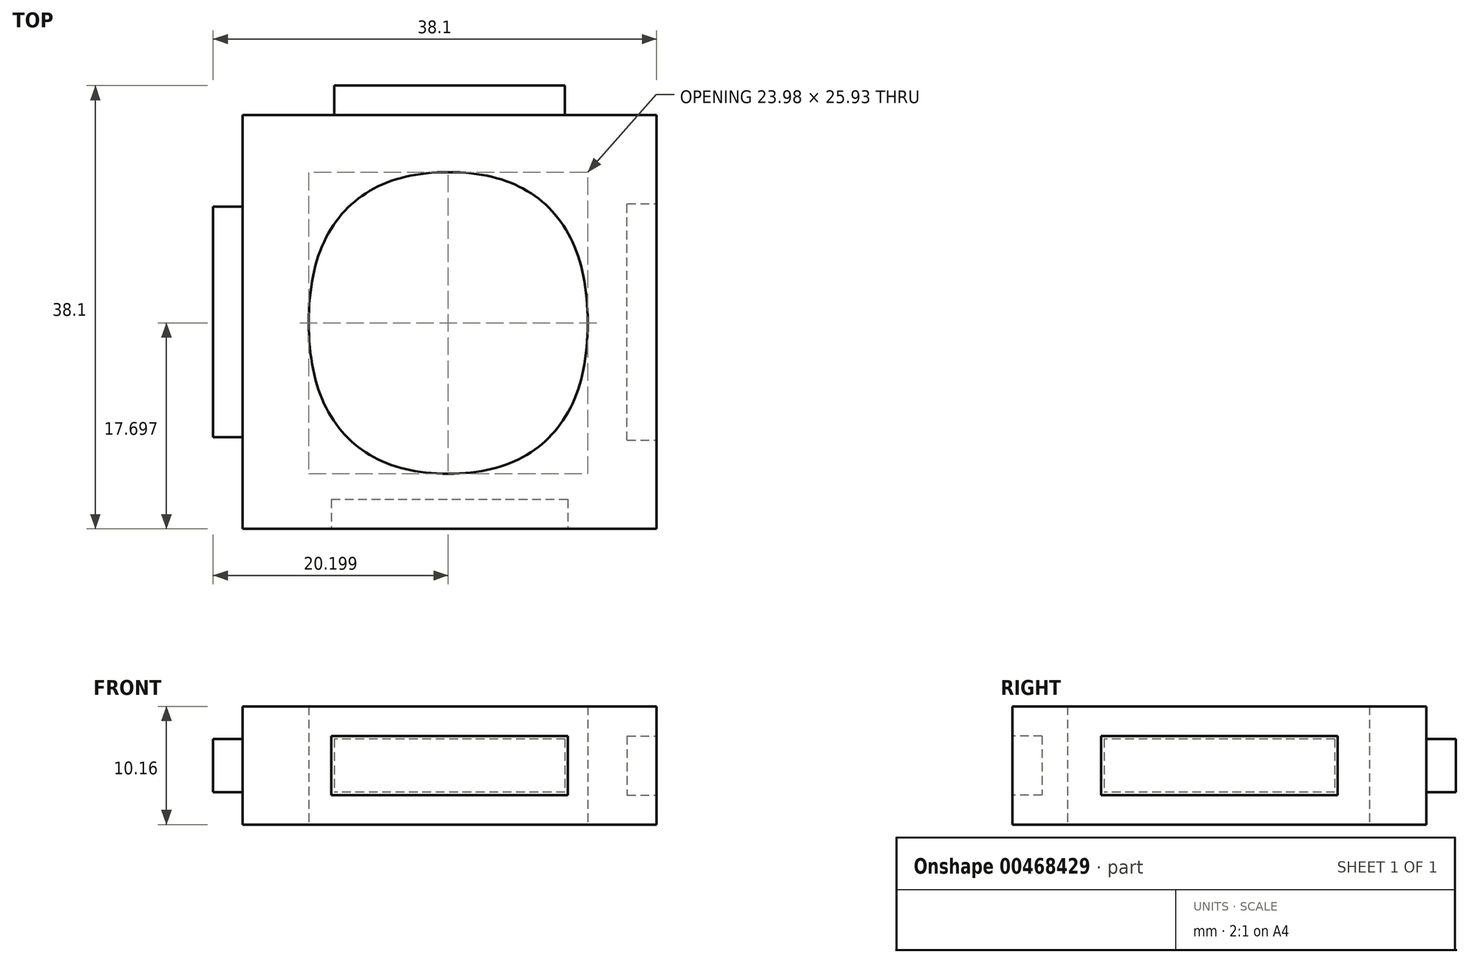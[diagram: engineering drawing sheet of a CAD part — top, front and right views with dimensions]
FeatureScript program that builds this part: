
annotation { "Feature Type Name" : "Feature", "Feature Type Description" : "" }
export const myFeature = defineFeature(function(context is Context, id is Id, definition is map)
    precondition{}
    {
        {
            var Q0;
            Q0=qCreatedBy(makeId("Top.planeOp"),FACE);
            var sketch = newSketch(context, id + "F0", { "sketchPlane" : qUnion([Q0])});
            skLineSegment(sketch, "E0.bottom", {"start": v(-17.78, 17.78) * mm, "end": v(17.78, 17.78) * mm});
            skLineSegment(sketch, "E0.top", {"start": v(-17.78, -17.78) * mm, "end": v(17.78, -17.78) * mm});
            skLineSegment(sketch, "E0.left", {"start": v(-17.78, 17.78) * mm, "end": v(-17.78, -17.78) * mm});
            skLineSegment(sketch, "E0.right", {"start": v(17.78, 17.78) * mm, "end": v(17.78, -17.78) * mm});
            skText(sketch, "E1", { "text": "O", "fontName": "OpenSans-Bold.ttf"});
            const initialGuessF0  = {"E1": [-0.01416, -0.0127, 1, 0, 0.0254]};
            skSetInitialGuess(sketch, initialGuessF0);
            skSolve(sketch);
        }
        {
            var Q0;
            Q0=qSketchRegion(id+"F0",true);
            extrude(context, id + "F1", {"entities" : qUnion([Q0]), "endBound" : BoundingType.SYMMETRIC, "depth" : 10.16 * mm});
        }
        {
            var Q0;
            Q0=makeQuery(id+"F1.opExtrude","SWEPT_FACE",FACE,{"disambiguationData":[OSD([sQuery(id+"F0.wireOp",EDGE,"E0.bottom")])]});
            var sketch = newSketch(context, id + "F2", { "sketchPlane" : qUnion([Q0])});
            skLineSegment(sketch, "E2.bottom", {"start": v(-9.9, 2.29) * mm, "end": v(9.9, 2.29) * mm});
            skLineSegment(sketch, "E2.top", {"start": v(-9.9, -2.29) * mm, "end": v(9.9, -2.29) * mm});
            skLineSegment(sketch, "E2.left", {"start": v(-9.9, 2.29) * mm, "end": v(-9.9, -2.29) * mm});
            skLineSegment(sketch, "E2.right", {"start": v(9.9, 2.29) * mm, "end": v(9.9, -2.29) * mm});
            skSolve(sketch);
        }
        {
            var Q0;
            Q0=qSketchRegion(id+"F2",true);
            extrude(context, id + "F3", {"entities" : qUnion([Q0]), "operationType" : NewBodyOperationType.ADD, "depth" : 2.54 * mm});
        }
        {
            var Q0;
            Q0=makeQuery(id+"F1.opExtrude","SWEPT_FACE",FACE,{"disambiguationData":[OSD([sQuery(id+"F0.wireOp",EDGE,"E0.left")])]});
            var sketch = newSketch(context, id + "F4", { "sketchPlane" : qUnion([Q0])});
            skLineSegment(sketch, "E3.bottom", {"start": v(-9.9, 2.29) * mm, "end": v(9.9, 2.29) * mm});
            skLineSegment(sketch, "E3.top", {"start": v(-9.9, -2.29) * mm, "end": v(9.9, -2.29) * mm});
            skLineSegment(sketch, "E3.left", {"start": v(-9.9, 2.29) * mm, "end": v(-9.9, -2.29) * mm});
            skLineSegment(sketch, "E3.right", {"start": v(9.9, 2.29) * mm, "end": v(9.9, -2.29) * mm});
            skSolve(sketch);
        }
        {
            var Q0;
            Q0=qSketchRegion(id+"F4",true);
            extrude(context, id + "F5", {"entities" : qUnion([Q0]), "operationType" : NewBodyOperationType.ADD, "depth" : 2.54 * mm});
        }
        {
            var Q0;
            Q0=makeQuery(id+"F1.opExtrude","SWEPT_FACE",FACE,{"disambiguationData":[OSD([sQuery(id+"F0.wireOp",EDGE,"E0.top")])]});
            var sketch = newSketch(context, id + "F6", { "sketchPlane" : qUnion([Q0])});
            skLineSegment(sketch, "E4.bottom", {"start": v(-10.16, 2.54) * mm, "end": v(10.16, 2.54) * mm});
            skLineSegment(sketch, "E4.top", {"start": v(-10.16, -2.54) * mm, "end": v(10.16, -2.54) * mm});
            skLineSegment(sketch, "E4.left", {"start": v(-10.16, 2.54) * mm, "end": v(-10.16, -2.54) * mm});
            skLineSegment(sketch, "E4.right", {"start": v(10.16, 2.54) * mm, "end": v(10.16, -2.54) * mm});
            skSolve(sketch);
        }
        {
            var Q0;
            Q0=qSketchRegion(id+"F6",true);
            extrude(context, id + "F7", {"entities" : qUnion([Q0]), "operationType" : NewBodyOperationType.REMOVE, "oppositeDirection" : true, "depth" : 2.54 * mm});
        }
        {
            var Q0;
            Q0=makeQuery(id+"F1.opExtrude","SWEPT_FACE",FACE,{"disambiguationData":[OSD([sQuery(id+"F0.wireOp",EDGE,"E0.right")])]});
            var sketch = newSketch(context, id + "F8", { "sketchPlane" : qUnion([Q0])});
            skLineSegment(sketch, "E5.bottom", {"start": v(-10.16, 2.54) * mm, "end": v(10.16, 2.54) * mm});
            skLineSegment(sketch, "E5.top", {"start": v(-10.16, -2.54) * mm, "end": v(10.16, -2.54) * mm});
            skLineSegment(sketch, "E5.left", {"start": v(-10.16, 2.54) * mm, "end": v(-10.16, -2.54) * mm});
            skLineSegment(sketch, "E5.right", {"start": v(10.16, 2.54) * mm, "end": v(10.16, -2.54) * mm});
            skSolve(sketch);
        }
        {
            var Q0;
            Q0=qSketchRegion(id+"F8",true);
            extrude(context, id + "F9", {"entities" : qUnion([Q0]), "operationType" : NewBodyOperationType.REMOVE, "oppositeDirection" : true, "depth" : 2.54 * mm});
        }
    });
